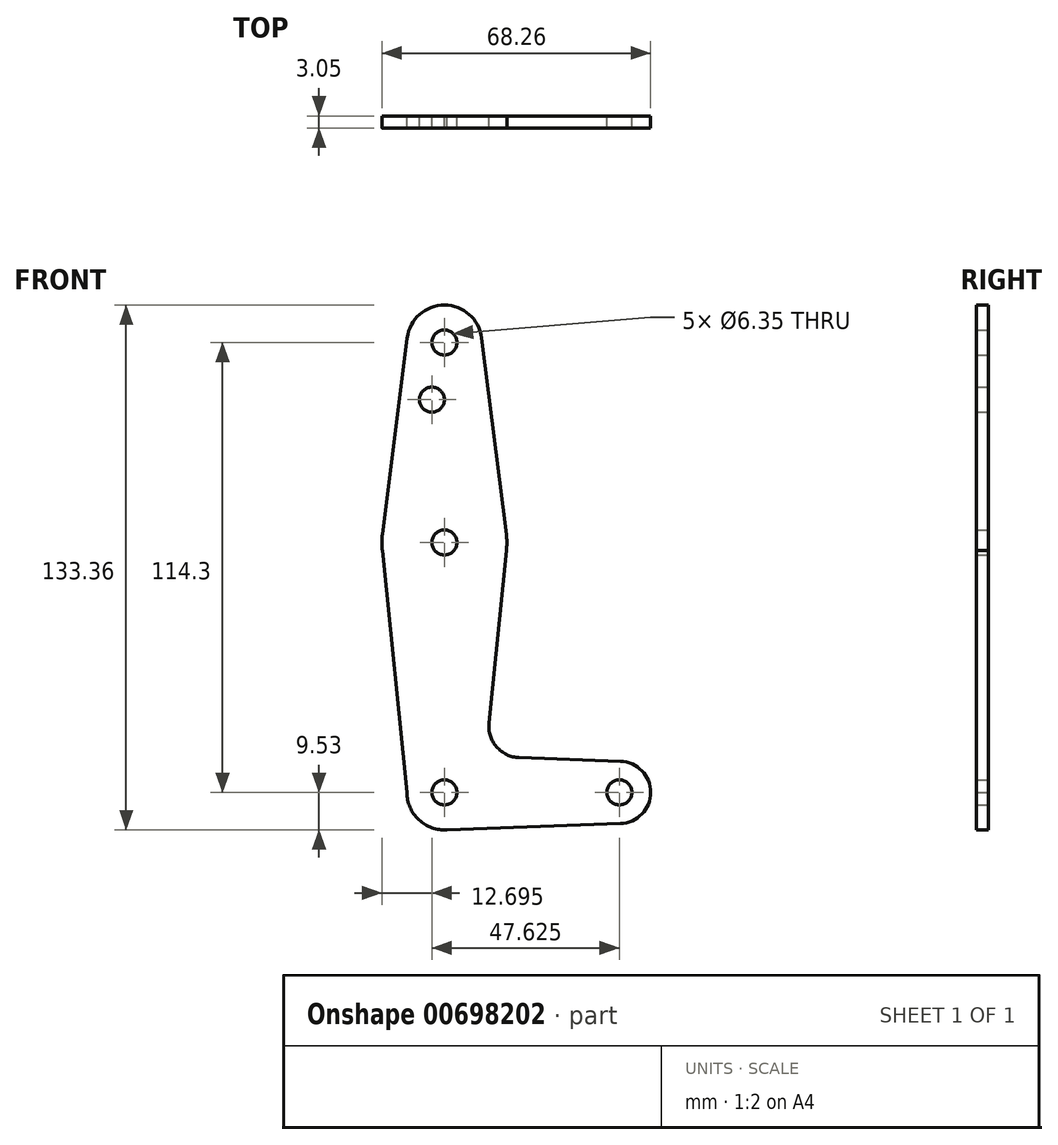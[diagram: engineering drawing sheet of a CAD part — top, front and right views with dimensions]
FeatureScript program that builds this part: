
annotation { "Feature Type Name" : "Feature", "Feature Type Description" : "" }
export const myFeature = defineFeature(function(context is Context, id is Id, definition is map)
    precondition{}
    {
        {
            var Q0;
            Q0=qCreatedBy(makeId("Front.planeOp"),FACE);
            var sketch = newSketch(context, id + "F0", { "sketchPlane" : qUnion([Q0])});
            skLineSegment(sketch, "E0", {"start": v(0, 114.3) * mm, "end": v(0, 63.5) * mm});
            skLineSegment(sketch, "E1", {"start": v(0, 63.5) * mm, "end": v(0, 0) * mm});
            skLineSegment(sketch, "E2", {"start": v(0, 0) * mm, "end": v(44.45, 0) * mm});
            skCircle(sketch, "E3", {"center": v(0, 114.3) * mm, "radius": 9.53 * mm});
            skCircle(sketch, "E4", {"center": v(0, 63.5) * mm, "radius": 15.88 * mm});
            skCircle(sketch, "E5", {"center": v(0, 0) * mm, "radius": 9.53 * mm});
            skCircle(sketch, "E6", {"center": v(44.45, 0) * mm, "radius": 7.94 * mm});
            skLineSegment(sketch, "E7", {"start": v(-9.45, 115.5) * mm, "end": v(-15.75, 65.48) * mm});
            skLineSegment(sketch, "E8", {"start": v(9.45, 115.5) * mm, "end": v(15.75, 65.48) * mm});
            skLineSegment(sketch, "E9", {"start": v(-9.52, 0) * mm, "end": v(-15.75, 61.52) * mm});
            skLineSegment(sketch, "E10", {"start": v(15.75, 61.52) * mm, "end": v(11.34, 17.59) * mm});
            skLineSegment(sketch, "E11", {"start": v(18.97, 8.85) * mm, "end": v(44.73, 7.93) * mm});
            skLineSegment(sketch, "E12", {"start": v(0, -9.52) * mm, "end": v(44.73, -7.93) * mm});
            skCircle(sketch, "E13", {"center": v(-3.17, 99.77) * mm, "radius": 3.18 * mm});
            skCircle(sketch, "E14", {"center": v(0, 114.3) * mm, "radius": 3.18 * mm});
            skCircle(sketch, "E15", {"center": v(0, 63.5) * mm, "radius": 3.18 * mm});
            skCircle(sketch, "E16", {"center": v(0, 0) * mm, "radius": 3.18 * mm});
            skCircle(sketch, "E17", {"center": v(44.45, 0) * mm, "radius": 3.18 * mm});
            skArc(sketch, "E18.filletArc", {"start": v(11.34, 17.59) * mm, "mid": v(13.26, 11.57) * mm, "end": v(18.97, 8.85) * mm});
            skSolve(sketch);
        }
        {
            var Q0;
            Q0 = qSketchRegion(id + "F0", true);
            var Q1;
            {var subQ0=sQuery(id+"F0.wireOp",EDGE,"E5");var subQ1=sQuery(id+"F0.wireOp",EDGE,"E1");var subQ2=makeQuery(id+"F0.imprint","INTERSECT",VERTEX,{"derivedFrom":[subQ1,subQ0]});Q1=makeQuery(id+"F0.imprint","IMPRINT",FACE,{"disambiguationData":[TD([[makeQuery(id+"F0.imprint","IMPRINT",EDGE,{"disambiguationData":[TD([[subQ2,-1.0]])],"derivedFrom":subQ1}),1.0]])]});}
            extrude(context, id + "F1", {"entities" : qUnion([Q0, Q1]), "depth" : 3.05 * mm, "offsetDistance" : 25.4 * mm});
        }
    });
